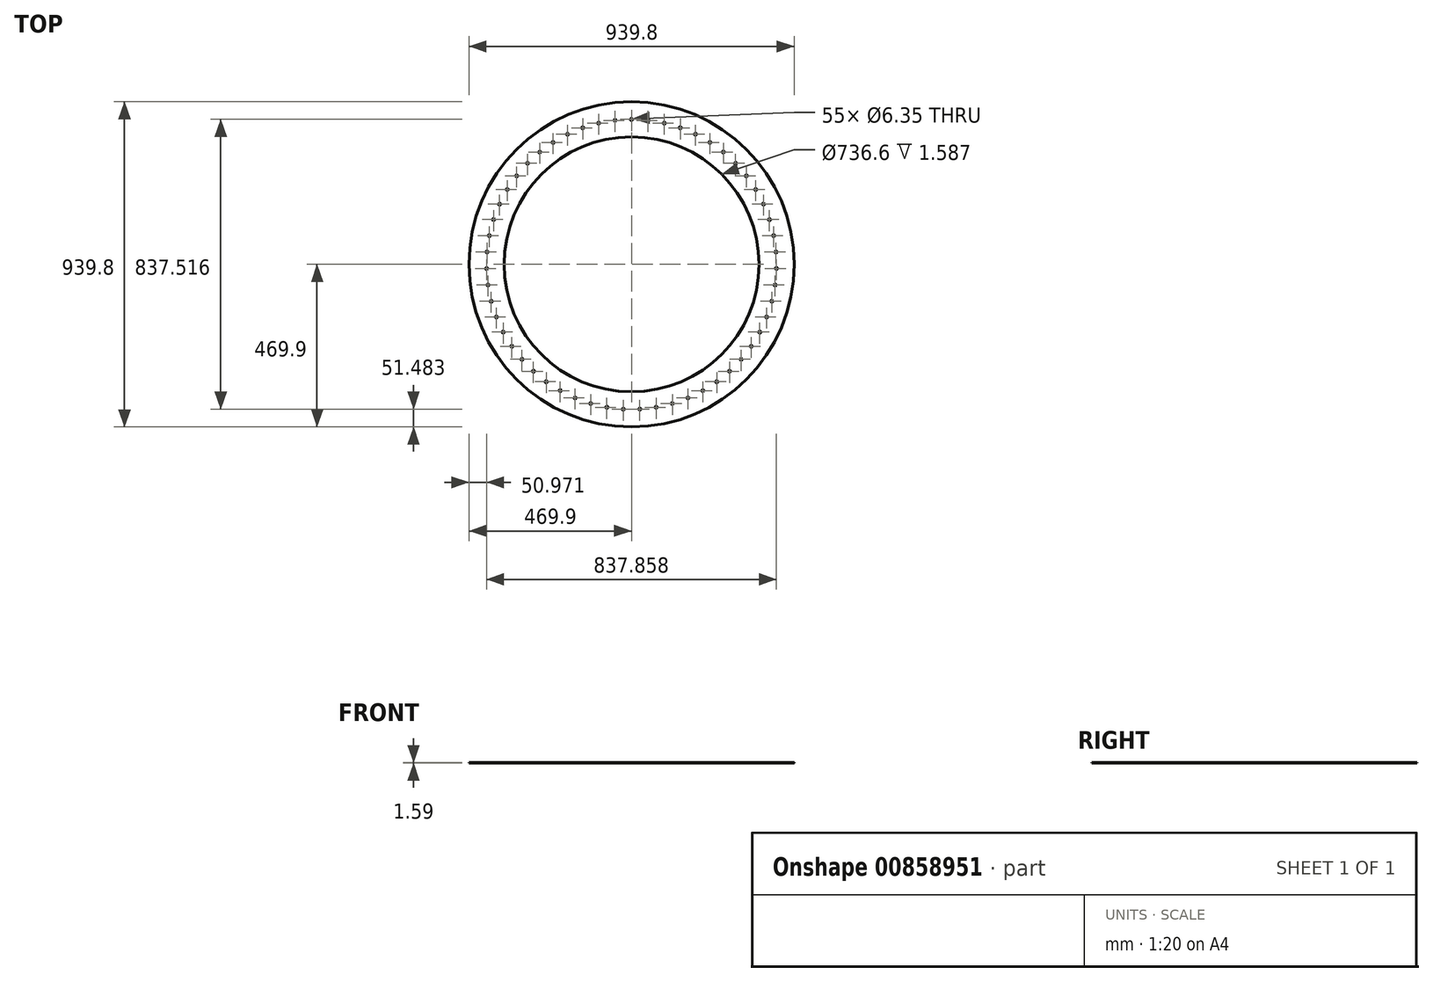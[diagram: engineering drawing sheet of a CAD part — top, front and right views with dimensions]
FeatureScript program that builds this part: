
annotation { "Feature Type Name" : "Feature", "Feature Type Description" : "" }
export const myFeature = defineFeature(function(context is Context, id is Id, definition is map)
    precondition{}
    {
        {
            var Q0;
            Q0=qCreatedBy(makeId("Top.planeOp"),FACE);
            var sketch = newSketch(context, id + "F0", { "sketchPlane" : qUnion([Q0])});
            skCircle(sketch, "E0", {"center": v(0, 0) * mm, "radius": 469.9 * mm});
            skCircle(sketch, "E1", {"center": v(0, 0) * mm, "radius": 368.3 * mm});
            skSolve(sketch);
        }
        {
            var Q0;
            Q0=makeQuery(id+"F0.imprint","IMPRINT",FACE,{"disambiguationData":[TD([[makeQuery(id+"F0.imprint","IMPRINT",EDGE,{"derivedFrom":sQuery(id+"F0.wireOp",EDGE,"E0")}),1.0]])]});
            extrude(context, id + "F1", {"entities" : qUnion([Q0]), "depth" : 1.59 * mm, "offsetDistance" : 25.4 * mm});
        }
        {
            var Q0;
            Q0=makeQuery(id+"F1.opExtrude","CAP_FACE",FACE,{"disambiguationData":[OSD([sQuery(id+"F0.wireOp",EDGE,"E0"),sQuery(id+"F0.wireOp",EDGE,"E1")])],"isStart":false});
            var sketch = newSketch(context, id + "F2", { "sketchPlane" : qUnion([Q0])});
            skLineSegment(sketch, "E2", {"start": v(0, 0) * mm, "end": v(0, 419.1) * mm, "construction": true});
            skCircle(sketch, "E3", {"center": v(0, 419.1) * mm, "radius": 3.18 * mm});
            skCircle(sketch, "E4.1.0", {"center": v(-47.77, 416.37) * mm, "radius": 3.18 * mm});
            skCircle(sketch, "E4.2.0", {"center": v(-94.92, 408.2) * mm, "radius": 3.18 * mm});
            skCircle(sketch, "E4.3.0", {"center": v(-140.84, 394.73) * mm, "radius": 3.18 * mm});
            skCircle(sketch, "E4.4.0", {"center": v(-184.92, 376.1) * mm, "radius": 3.18 * mm});
            skCircle(sketch, "E4.5.0", {"center": v(-226.58, 352.57) * mm, "radius": 3.18 * mm});
            skCircle(sketch, "E4.6.0", {"center": v(-265.3, 324.44) * mm, "radius": 3.18 * mm});
            skCircle(sketch, "E4.7.0", {"center": v(-300.55, 292.09) * mm, "radius": 3.18 * mm});
            skCircle(sketch, "E4.8.0", {"center": v(-331.89, 255.92) * mm, "radius": 3.18 * mm});
            skCircle(sketch, "E4.9.0", {"center": v(-358.9, 216.42) * mm, "radius": 3.18 * mm});
            skCircle(sketch, "E4.10.0", {"center": v(-381.23, 174.1) * mm, "radius": 3.18 * mm});
            skCircle(sketch, "E4.11.0", {"center": v(-398.59, 129.5) * mm, "radius": 3.18 * mm});
            skCircle(sketch, "E4.12.0", {"center": v(-410.75, 83.23) * mm, "radius": 3.18 * mm});
            skCircle(sketch, "E4.13.0", {"center": v(-417.56, 35.86) * mm, "radius": 3.18 * mm});
            skCircle(sketch, "E4.14.0", {"center": v(-418.93, -11.97) * mm, "radius": 3.18 * mm});
            skCircle(sketch, "E4.15.0", {"center": v(-414.83, -59.64) * mm, "radius": 3.18 * mm});
            skCircle(sketch, "E4.16.0", {"center": v(-405.33, -106.54) * mm, "radius": 3.18 * mm});
            skCircle(sketch, "E4.17.0", {"center": v(-390.54, -152.05) * mm, "radius": 3.18 * mm});
            skCircle(sketch, "E4.18.0", {"center": v(-370.67, -195.58) * mm, "radius": 3.18 * mm});
            skCircle(sketch, "E4.19.0", {"center": v(-345.96, -236.56) * mm, "radius": 3.18 * mm});
            skCircle(sketch, "E4.20.0", {"center": v(-316.73, -274.45) * mm, "radius": 3.18 * mm});
            skCircle(sketch, "E4.21.0", {"center": v(-283.38, -308.77) * mm, "radius": 3.18 * mm});
            skCircle(sketch, "E4.22.0", {"center": v(-246.34, -339.06) * mm, "radius": 3.17 * mm});
            skCircle(sketch, "E4.23.0", {"center": v(-206.09, -364.93) * mm, "radius": 3.18 * mm});
            skCircle(sketch, "E4.24.0", {"center": v(-163.14, -386.04) * mm, "radius": 3.17 * mm});
            skCircle(sketch, "E4.25.0", {"center": v(-118.07, -402.12) * mm, "radius": 3.18 * mm});
            skCircle(sketch, "E4.26.0", {"center": v(-71.47, -412.96) * mm, "radius": 3.18 * mm});
            skCircle(sketch, "E4.27.0", {"center": v(-23.93, -418.42) * mm, "radius": 3.18 * mm});
            skCircle(sketch, "E4.28.0", {"center": v(23.93, -418.42) * mm, "radius": 3.17 * mm});
            skCircle(sketch, "E4.29.0", {"center": v(71.47, -412.96) * mm, "radius": 3.18 * mm});
            skCircle(sketch, "E4.30.0", {"center": v(118.07, -402.12) * mm, "radius": 3.18 * mm});
            skCircle(sketch, "E4.31.0", {"center": v(163.14, -386.04) * mm, "radius": 3.18 * mm});
            skCircle(sketch, "E4.32.0", {"center": v(206.09, -364.93) * mm, "radius": 3.17 * mm});
            skCircle(sketch, "E4.33.0", {"center": v(246.34, -339.06) * mm, "radius": 3.18 * mm});
            skCircle(sketch, "E4.34.0", {"center": v(283.38, -308.77) * mm, "radius": 3.17 * mm});
            skCircle(sketch, "E4.35.0", {"center": v(316.73, -274.45) * mm, "radius": 3.18 * mm});
            skCircle(sketch, "E4.36.0", {"center": v(345.96, -236.56) * mm, "radius": 3.18 * mm});
            skCircle(sketch, "E4.37.0", {"center": v(370.67, -195.58) * mm, "radius": 3.18 * mm});
            skCircle(sketch, "E4.38.0", {"center": v(390.54, -152.05) * mm, "radius": 3.18 * mm});
            skCircle(sketch, "E4.39.0", {"center": v(405.33, -106.54) * mm, "radius": 3.18 * mm});
            skCircle(sketch, "E4.40.0", {"center": v(414.83, -59.64) * mm, "radius": 3.18 * mm});
            skCircle(sketch, "E4.41.0", {"center": v(418.93, -11.97) * mm, "radius": 3.18 * mm});
            skCircle(sketch, "E4.42.0", {"center": v(417.56, 35.86) * mm, "radius": 3.18 * mm});
            skCircle(sketch, "E4.43.0", {"center": v(410.75, 83.23) * mm, "radius": 3.18 * mm});
            skCircle(sketch, "E4.44.0", {"center": v(398.59, 129.5) * mm, "radius": 3.18 * mm});
            skCircle(sketch, "E4.45.0", {"center": v(381.23, 174.1) * mm, "radius": 3.17 * mm});
            skCircle(sketch, "E4.46.0", {"center": v(358.9, 216.42) * mm, "radius": 3.18 * mm});
            skCircle(sketch, "E4.47.0", {"center": v(331.89, 255.92) * mm, "radius": 3.17 * mm});
            skCircle(sketch, "E4.48.0", {"center": v(300.55, 292.09) * mm, "radius": 3.17 * mm});
            skCircle(sketch, "E4.49.0", {"center": v(265.3, 324.44) * mm, "radius": 3.18 * mm});
            skCircle(sketch, "E4.50.0", {"center": v(226.58, 352.57) * mm, "radius": 3.18 * mm});
            skCircle(sketch, "E4.51.0", {"center": v(184.92, 376.1) * mm, "radius": 3.18 * mm});
            skCircle(sketch, "E4.52.0", {"center": v(140.84, 394.73) * mm, "radius": 3.18 * mm});
            skCircle(sketch, "E4.53.0", {"center": v(94.92, 408.2) * mm, "radius": 3.18 * mm});
            skCircle(sketch, "E4.54.0", {"center": v(47.77, 416.37) * mm, "radius": 3.18 * mm});
            skPoint(sketch, "E4.center", {"position": v(0, 0) * mm});
            skSolve(sketch);
        }
        {
            var Q0;
            Q0 = qSketchRegion(id + "F2", true);
            extrude(context, id + "F3", {"entities" : qUnion([Q0]), "operationType" : NewBodyOperationType.REMOVE, "oppositeDirection" : true, "depth" : 25.4 * mm, "offsetDistance" : 25.4 * mm});
        }
    });
